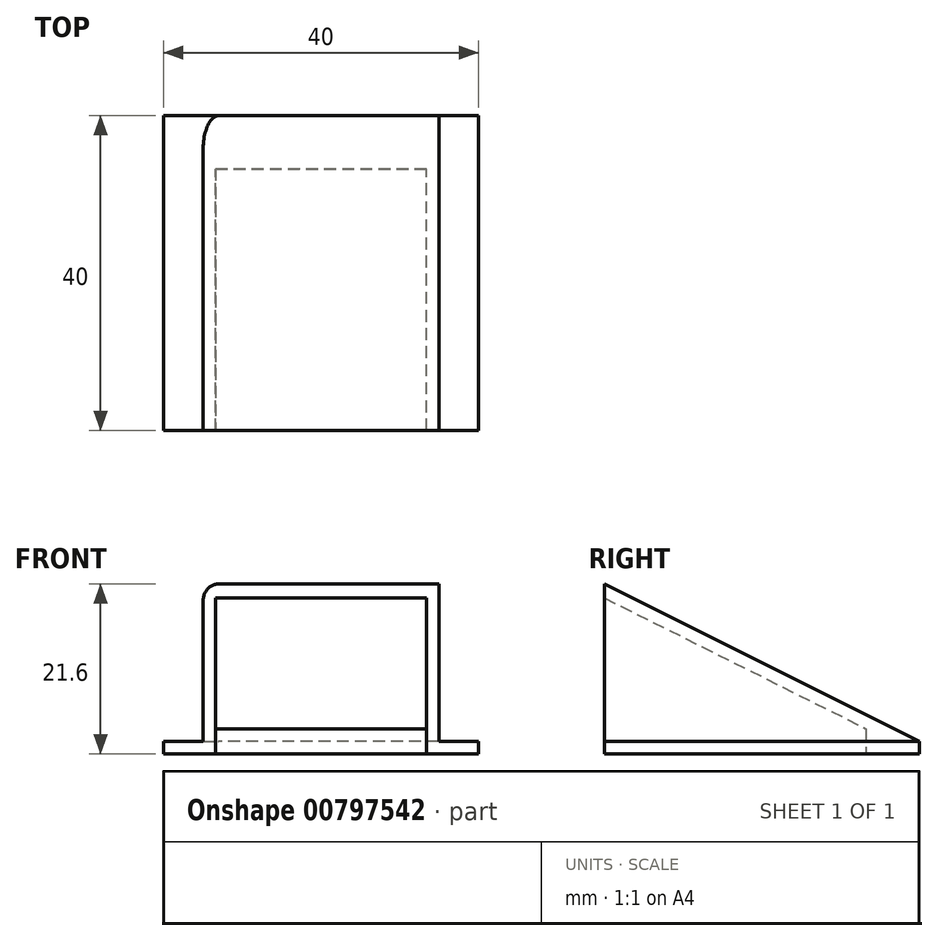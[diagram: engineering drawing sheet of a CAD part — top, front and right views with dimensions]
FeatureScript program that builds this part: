
annotation { "Feature Type Name" : "Feature", "Feature Type Description" : "" }
export const myFeature = defineFeature(function(context is Context, id is Id, definition is map)
    precondition{}
    {
        {
            var Q0;
            Q0=qCreatedBy(makeId("Top.planeOp"),FACE);
            var sketch = newSketch(context, id + "F0", { "sketchPlane" : qUnion([Q0])});
            skLineSegment(sketch, "E0.bottom", {"start": v(15, -20) * mm, "end": v(-15, -20) * mm});
            skLineSegment(sketch, "E0.top", {"start": v(15, 20) * mm, "end": v(-15, 20) * mm});
            skLineSegment(sketch, "E0.left", {"start": v(15, -20) * mm, "end": v(15, 20) * mm});
            skLineSegment(sketch, "E0.right", {"start": v(-15, -20) * mm, "end": v(-15, 20) * mm});
            skPoint(sketch, "E0.middle", {"position": v(0, 0) * mm});
            skSolve(sketch);
        }
        {
            var Q0;
            Q0 = qSketchRegion(id + "F0", true);
            extrude(context, id + "F1", {"entities" : qUnion([Q0]), "depth" : 20 * mm, "offsetDistance" : 25 * mm});
        }
        {
            var Q0;
            Q0=makeQuery(id+"F1.opExtrude","SWEPT_FACE",FACE,{"disambiguationData":[OSD([sQuery(id+"F0.wireOp",EDGE,"E0.left")])]});
            var sketch = newSketch(context, id + "F2", { "sketchPlane" : qUnion([Q0])});
            skLineSegment(sketch, "E1", {"start": v(-20, 20) * mm, "end": v(20, 0) * mm});
            skLineSegment(sketch, "E2", {"start": v(20, 0) * mm, "end": v(20, 20) * mm});
            skLineSegment(sketch, "E3", {"start": v(20, 20) * mm, "end": v(-20, 20) * mm});
            skSolve(sketch);
        }
        {
            var Q0;
            Q0 = qSketchRegion(id + "F2", true);
            extrude(context, id + "F3", {"entities" : qUnion([Q0]), "operationType" : NewBodyOperationType.REMOVE, "endBound" : BoundingType.THROUGH_ALL, "oppositeDirection" : true, "depth" : 30 * mm, "offsetDistance" : 25 * mm});
        }
        {
            var Q0;
            Q0=makeQuery(id+"F1.opExtrude","SWEPT_FACE",FACE,{"disambiguationData":[OSD([sQuery(id+"F0.wireOp",EDGE,"E0.bottom")])]});
            shell(context, id + "F4", {"entities" : qUnion([Q0]), "thickness" : 1.6 * mm});
        }
        {
            var Q0;
            Q0=makeQuery(id+"F1.opExtrude","CAP_FACE",FACE,{"disambiguationData":[OSD([sQuery(id+"F0.wireOp",EDGE,"E0.bottom"),sQuery(id+"F0.wireOp",EDGE,"E0.top"),sQuery(id+"F0.wireOp",EDGE,"E0.left"),sQuery(id+"F0.wireOp",EDGE,"E0.right")])],"isStart":true});
            var sketch = newSketch(context, id + "F5", { "sketchPlane" : qUnion([Q0])});
            skLineSegment(sketch, "E4.bottom", {"start": v(-13.4, 20) * mm, "end": v(13.4, 20) * mm});
            skLineSegment(sketch, "E4.top", {"start": v(-13.4, -13.2) * mm, "end": v(13.4, -13.2) * mm});
            skLineSegment(sketch, "E4.left", {"start": v(-13.4, 20) * mm, "end": v(-13.4, -13.2) * mm});
            skLineSegment(sketch, "E4.right", {"start": v(13.4, 20) * mm, "end": v(13.4, -13.2) * mm});
            skSolve(sketch);
        }
        {
            var Q0;
            Q0 = qSketchRegion(id + "F5", true);
            extrude(context, id + "F6", {"entities" : qUnion([Q0]), "operationType" : NewBodyOperationType.REMOVE, "oppositeDirection" : true, "depth" : 1.6 * mm, "offsetDistance" : 25 * mm});
        }
        {
            var Q0;
            Q0=makeQuery(id+"F1.opExtrude","CAP_FACE",FACE,{"disambiguationData":[OSD([sQuery(id+"F0.wireOp",EDGE,"E0.bottom"),sQuery(id+"F0.wireOp",EDGE,"E0.top"),sQuery(id+"F0.wireOp",EDGE,"E0.left"),sQuery(id+"F0.wireOp",EDGE,"E0.right")])],"isStart":true});
            var sketch = newSketch(context, id + "F7", { "sketchPlane" : qUnion([Q0])});
            skLineSegment(sketch, "E5.bottom", {"start": v(-20, -20) * mm, "end": v(20, -20) * mm});
            skLineSegment(sketch, "E5.top", {"start": v(-20, 20) * mm, "end": v(-13.4, 20) * mm});
            skLineSegment(sketch, "E5.left", {"start": v(-20, -20) * mm, "end": v(-20, 20) * mm});
            skLineSegment(sketch, "E5.right", {"start": v(20, -20) * mm, "end": v(20, 20) * mm});
            skLineSegment(sketch, "E6", {"start": v(-13.4, 20) * mm, "end": v(-13.4, -13.2) * mm});
            skLineSegment(sketch, "E7", {"start": v(-13.4, -13.2) * mm, "end": v(13.4, -13.2) * mm});
            skLineSegment(sketch, "E8", {"start": v(13.4, -13.2) * mm, "end": v(13.4, 20) * mm});
            skLineSegment(sketch, "E9.trimOffspring", {"start": v(13.4, 20) * mm, "end": v(20, 20) * mm});
            skSolve(sketch);
        }
        {
            var Q0;
            Q0 = qSketchRegion(id + "F7", true);
            extrude(context, id + "F8", {"entities" : qUnion([Q0]), "operationType" : NewBodyOperationType.ADD, "depth" : 1.6 * mm, "offsetDistance" : 25 * mm});
        }
        {
            var Q0;
            Q0=makeQuery(id+"F3.boolean.opBoolean","INTERSECT",EDGE,{"derivedFrom":[makeQuery(id+"F1.opExtrude","SWEPT_FACE",FACE,{"disambiguationData":[OSD([sQuery(id+"F0.wireOp",EDGE,"E0.right")])]}),makeQuery(id+"F3.opExtrude","SWEPT_FACE",FACE,{"disambiguationData":[OSD([sQuery(id+"F2.wireOp",EDGE,"E1")])]})]});
            var Q1;
            Q1=makeQuery(id+"F3.boolean.opBoolean","COPY",EDGE,{"derivedFrom":makeQuery(id+"F3.opExtrude","CAP_EDGE",EDGE,{"disambiguationData":[OSD([sQuery(id+"F2.wireOp",EDGE,"E1")])],"isStart":true})});
            fillet(context, id + "F9", {"entities" : qUnion([Q0, Q1]), "radius" : 2 * mm, "tangentPropagation" : true, "allowEdgeOverflow" : false});
        }
    });
